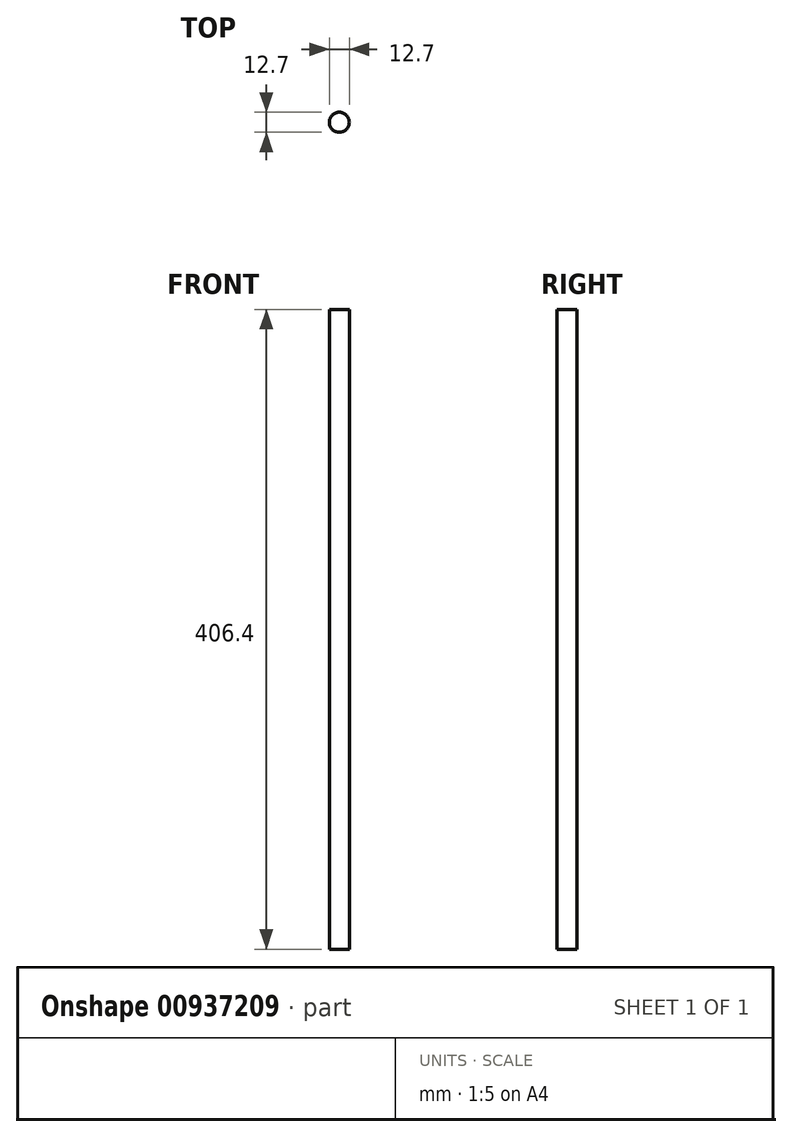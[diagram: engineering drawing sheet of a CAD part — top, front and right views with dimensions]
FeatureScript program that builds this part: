
annotation { "Feature Type Name" : "Feature", "Feature Type Description" : "" }
export const myFeature = defineFeature(function(context is Context, id is Id, definition is map)
    precondition{}
    {
        {
            var Q0;
            Q0=qCreatedBy(makeId("Top.planeOp"),FACE);
            var sketch = newSketch(context, id + "F0", { "sketchPlane" : qUnion([Q0])});
            skCircle(sketch, "E0", {"center": v(0, 0) * mm, "radius": 6.35 * mm});
            skSolve(sketch);
        }
        {
            var Q0;
            Q0=makeQuery(id+"F0.imprint","IMPRINT",FACE,{"disambiguationData":[TD([[makeQuery(id+"F0.imprint","IMPRINT",EDGE,{"derivedFrom":sQuery(id+"F0.wireOp",EDGE,"E0")}),1.0]])]});
            extrude(context, id + "F1", {"entities" : qUnion([Q0]), "depth" : 406.4 * mm, "offsetDistance" : 25.4 * mm});
        }
    });
